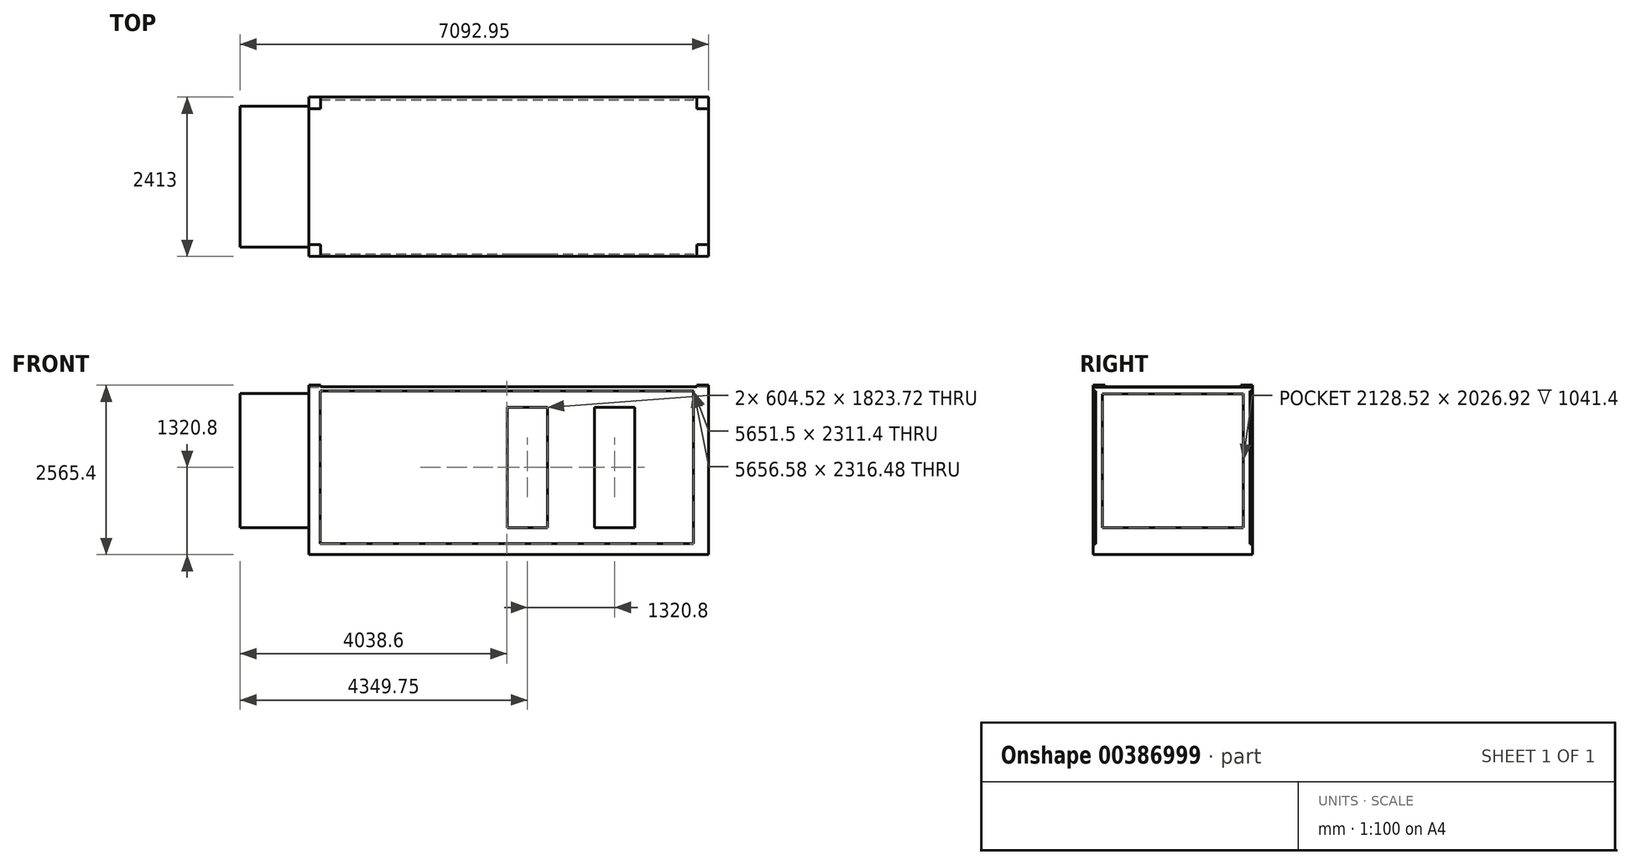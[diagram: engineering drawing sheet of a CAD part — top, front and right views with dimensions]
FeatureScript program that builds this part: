
annotation { "Feature Type Name" : "Feature", "Feature Type Description" : "" }
export const myFeature = defineFeature(function(context is Context, id is Id, definition is map)
    precondition{}
    {
        {
            var Q0;
            Q0=qCreatedBy(makeId("Front.planeOp"),FACE);
            var sketch = newSketch(context, id + "F0", { "sketchPlane" : qUnion([Q0])});
            skLineSegment(sketch, "E0.bottom", {"start": v(0, 0) * mm, "end": v(5651.5, 0) * mm, "construction": true});
            skLineSegment(sketch, "E0.top", {"start": v(0, 2311.4) * mm, "end": v(5651.5, 2311.4) * mm, "construction": true});
            skLineSegment(sketch, "E0.left", {"start": v(0, 0) * mm, "end": v(0, 2311.4) * mm, "construction": true});
            skLineSegment(sketch, "E0.right", {"start": v(5651.5, 0) * mm, "end": v(5651.5, 2311.4) * mm, "construction": true});
            skLineSegment(sketch, "E1.bottom", {"start": v(-171.45, -165.1) * mm, "end": v(5880.1, -165.1) * mm});
            skLineSegment(sketch, "E1.top", {"start": v(-171.45, 2374.9) * mm, "end": v(5880.1, 2374.9) * mm});
            skLineSegment(sketch, "E1.left", {"start": v(-171.45, -165.1) * mm, "end": v(-171.45, 2374.9) * mm});
            skLineSegment(sketch, "E1.right", {"start": v(5880.1, -165.1) * mm, "end": v(5880.1, 2374.9) * mm});
            skSolve(sketch);
        }
        {
            var Q0;
            Q0=makeQuery(id+"F0.imprint","IMPRINT",FACE,{"disambiguationData":[TD([[makeQuery(id+"F0.imprint","IMPRINT",EDGE,{"derivedFrom":sQuery(id+"F0.wireOp",EDGE,"E0.bottom")}),-1.0]])]});
            var Q1;
            Q1=makeQuery(id+"F0.imprint","IMPRINT",FACE,{"disambiguationData":[TD([[makeQuery(id+"F0.imprint","IMPRINT",EDGE,{"derivedFrom":sQuery(id+"F0.wireOp",EDGE,"E1.bottom")}),1.0]])]});
            extrude(context, id + "F1", {"entities" : qUnion([Q0, Q1]), "depth" : 2413 * mm});
        }
        {
            var Q0;
            Q0=makeQuery(id+"F1.opExtrude","CAP_FACE",FACE,{"disambiguationData":[OSD([sQuery(id+"F0.wireOp",EDGE,"E1.bottom"),sQuery(id+"F0.wireOp",EDGE,"E1.top"),sQuery(id+"F0.wireOp",EDGE,"E1.left"),sQuery(id+"F0.wireOp",EDGE,"E1.right")])],"isStart":false});
            var sketch = newSketch(context, id + "F2", { "sketchPlane" : qUnion([Q0])});
            skLineSegment(sketch, "E2.0", {"start": v(0, 2311.4) * mm, "end": v(5651.5, 2311.4) * mm});
            skLineSegment(sketch, "E3.0", {"start": v(0, 0) * mm, "end": v(5651.5, 0) * mm});
            skLineSegment(sketch, "E4.0", {"start": v(5651.5, 0) * mm, "end": v(5651.5, 2311.4) * mm});
            skLineSegment(sketch, "E5.0", {"start": v(0, 0) * mm, "end": v(0, 2311.4) * mm});
            skSolve(sketch);
        }
        {
            var Q0;
            Q0=qSketchRegion(id+"F2",true);
            extrude(context, id + "F3", {"entities" : qUnion([Q0]), "operationType" : NewBodyOperationType.REMOVE, "oppositeDirection" : true, "depth" : 38.1 * mm});
        }
        {
            var Q0;
            Q0=makeQuery(id+"F0.imprint","IMPRINT",FACE,{"disambiguationData":[TD([[makeQuery(id+"F0.imprint","IMPRINT",EDGE,{"derivedFrom":sQuery(id+"F0.wireOp",EDGE,"E1.bottom")}),1.0]])]});
            var sketch = newSketch(context, id + "F4", { "sketchPlane" : qUnion([Q0])});
            skLineSegment(sketch, "E6.0", {"start": v(0, 2311.4) * mm, "end": v(5651.5, 2311.4) * mm});
            skLineSegment(sketch, "E7.0", {"start": v(5651.5, 0) * mm, "end": v(5651.5, 2311.4) * mm});
            skLineSegment(sketch, "E8.0", {"start": v(0, 0) * mm, "end": v(5651.5, 0) * mm});
            skLineSegment(sketch, "E9.0", {"start": v(0, 0) * mm, "end": v(0, 2311.4) * mm});
            skSolve(sketch);
        }
        {
            var Q0;
            Q0=qSketchRegion(id+"F4",true);
            extrude(context, id + "F5", {"entities" : qUnion([Q0]), "operationType" : NewBodyOperationType.REMOVE, "depth" : 38.1 * mm});
        }
        {
            var Q0;
            Q0=makeQuery(id+"F3.boolean.opBoolean","COPY",FACE,{"derivedFrom":makeQuery(id+"F3.opExtrude","CAP_FACE",FACE,{"disambiguationData":[OSD([sQuery(id+"F2.wireOp",EDGE,"E2.0"),sQuery(id+"F2.wireOp",EDGE,"E3.0"),sQuery(id+"F2.wireOp",EDGE,"E4.0"),sQuery(id+"F2.wireOp",EDGE,"E5.0")])],"isStart":false})});
            var sketch = newSketch(context, id + "F6", { "sketchPlane" : qUnion([Q0])});
            skLineSegment(sketch, "E10.bottom", {"start": v(2832.1, 2070.1) * mm, "end": v(3441.7, 2070.1) * mm});
            skLineSegment(sketch, "E10.top", {"start": v(2832.1, 241.3) * mm, "end": v(3441.7, 241.3) * mm});
            skLineSegment(sketch, "E10.left", {"start": v(2832.1, 2070.1) * mm, "end": v(2832.1, 241.3) * mm});
            skLineSegment(sketch, "E10.right", {"start": v(3441.7, 2070.1) * mm, "end": v(3441.7, 241.3) * mm});
            skLineSegment(sketch, "E11.bottom", {"start": v(4152.9, 2070.1) * mm, "end": v(4762.5, 2070.1) * mm});
            skLineSegment(sketch, "E11.top", {"start": v(4152.9, 241.3) * mm, "end": v(4762.5, 241.3) * mm});
            skLineSegment(sketch, "E11.left", {"start": v(4152.9, 2070.1) * mm, "end": v(4152.9, 241.3) * mm});
            skLineSegment(sketch, "E11.right", {"start": v(4762.5, 2070.1) * mm, "end": v(4762.5, 241.3) * mm});
            skLineSegment(sketch, "E12", {"start": v(3267.34, 2311.4) * mm, "end": v(3267.34, 2070.1) * mm, "construction": true});
            skLineSegment(sketch, "E13", {"start": v(4451.93, 241.3) * mm, "end": v(4451.93, 0) * mm, "construction": true});
            skLineSegment(sketch, "E14", {"start": v(2825.75, 2311.4) * mm, "end": v(2825.75, 0) * mm, "construction": true});
            skSolve(sketch);
        }
        {
            var Q0;
            Q0=qSketchRegion(id+"F6",true);
            extrude(context, id + "F7", {"entities" : qUnion([Q0]), "operationType" : NewBodyOperationType.ADD, "depth" : 25.4 * mm});
        }
        {
            var Q0;
            Q0=makeQuery(id+"F1.opExtrude","SWEPT_FACE",FACE,{"disambiguationData":[OSD([sQuery(id+"F0.wireOp",EDGE,"E1.left")])]});
            var sketch = newSketch(context, id + "F8", { "sketchPlane" : qUnion([Q0])});
            skLineSegment(sketch, "E15.bottom", {"start": v(139.7, 2273.3) * mm, "end": v(2273.3, 2273.3) * mm});
            skLineSegment(sketch, "E15.top", {"start": v(139.7, 241.3) * mm, "end": v(2273.3, 241.3) * mm});
            skLineSegment(sketch, "E15.left", {"start": v(139.7, 2273.3) * mm, "end": v(139.7, 241.3) * mm});
            skLineSegment(sketch, "E15.right", {"start": v(2273.3, 2273.3) * mm, "end": v(2273.3, 241.3) * mm});
            skSolve(sketch);
        }
        {
            var Q0;
            Q0=qSketchRegion(id+"F8",true);
            extrude(context, id + "F9", {"entities" : qUnion([Q0]), "operationType" : NewBodyOperationType.ADD, "depth" : 1041.4 * mm});
        }
        {
            var Q0;
            Q0=makeQuery(id+"F1.opExtrude","SWEPT_FACE",FACE,{"disambiguationData":[OSD([sQuery(id+"F0.wireOp",EDGE,"E1.top")])]});
            var sketch = newSketch(context, id + "F10", { "sketchPlane" : qUnion([Q0])});
            skLineSegment(sketch, "E16.bottom", {"start": v(-171.45, -2413) * mm, "end": v(6.35, -2413) * mm});
            skLineSegment(sketch, "E16.top", {"start": v(-171.45, -2235.2) * mm, "end": v(6.35, -2235.2) * mm});
            skLineSegment(sketch, "E16.left", {"start": v(-171.45, -2413) * mm, "end": v(-171.45, -2235.2) * mm});
            skLineSegment(sketch, "E16.right", {"start": v(6.35, -2413) * mm, "end": v(6.35, -2235.2) * mm});
            skLineSegment(sketch, "E17.bottom", {"start": v(-171.45, 0) * mm, "end": v(6.35, 0) * mm});
            skLineSegment(sketch, "E17.top", {"start": v(-171.45, -177.8) * mm, "end": v(6.35, -177.8) * mm});
            skLineSegment(sketch, "E17.left", {"start": v(-171.45, 0) * mm, "end": v(-171.45, -177.8) * mm});
            skLineSegment(sketch, "E17.right", {"start": v(6.35, 0) * mm, "end": v(6.35, -177.8) * mm});
            skLineSegment(sketch, "E18.bottom", {"start": v(5880.1, 0) * mm, "end": v(5702.3, 0) * mm});
            skLineSegment(sketch, "E18.top", {"start": v(5880.1, -177.8) * mm, "end": v(5702.3, -177.8) * mm});
            skLineSegment(sketch, "E18.left", {"start": v(5880.1, 0) * mm, "end": v(5880.1, -177.8) * mm});
            skLineSegment(sketch, "E18.right", {"start": v(5702.3, 0) * mm, "end": v(5702.3, -177.8) * mm});
            skLineSegment(sketch, "E19.bottom", {"start": v(5880.1, -2413) * mm, "end": v(5702.3, -2413) * mm});
            skLineSegment(sketch, "E19.top", {"start": v(5880.1, -2235.2) * mm, "end": v(5702.3, -2235.2) * mm});
            skLineSegment(sketch, "E19.left", {"start": v(5880.1, -2413) * mm, "end": v(5880.1, -2235.2) * mm});
            skLineSegment(sketch, "E19.right", {"start": v(5702.3, -2413) * mm, "end": v(5702.3, -2235.2) * mm});
            skSolve(sketch);
        }
        {
            var Q0;
            Q0=qSketchRegion(id+"F10",true);
            extrude(context, id + "F11", {"entities" : qUnion([Q0]), "operationType" : NewBodyOperationType.ADD, "depth" : 25.4 * mm});
        }
        {
            var Q0;
            Q0=makeQuery(id+"F11.boolean.opBoolean","MERGE",FACE,{"derivedFrom":[makeQuery(id+"F1.opExtrude","CAP_FACE",FACE,{"disambiguationData":[OSD([sQuery(id+"F0.wireOp",EDGE,"E1.bottom"),sQuery(id+"F0.wireOp",EDGE,"E1.top"),sQuery(id+"F0.wireOp",EDGE,"E1.left"),sQuery(id+"F0.wireOp",EDGE,"E1.right")])],"isStart":false}),makeQuery(id+"F11.opExtrude","SWEPT_FACE",FACE,{"disambiguationData":[OSD([sQuery(id+"F10.wireOp",EDGE,"E16.bottom")])]}),makeQuery(id+"F11.opExtrude","SWEPT_FACE",FACE,{"disambiguationData":[OSD([sQuery(id+"F10.wireOp",EDGE,"E19.bottom")])]})]});
            var sketch = newSketch(context, id + "F12", { "sketchPlane" : qUnion([Q0])});
            skLineSegment(sketch, "E20", {"start": v(5880.1, -12.7) * mm, "end": v(7404.1, -165.1) * mm});
            skLineSegment(sketch, "E21", {"start": v(7404.1, -165.1) * mm, "end": v(7404.1, -114.05) * mm});
            skLineSegment(sketch, "E22", {"start": v(7404.1, -114.05) * mm, "end": v(5880.1, 38.35) * mm});
            skLineSegment(sketch, "E23", {"start": v(5880.1, 38.35) * mm, "end": v(5880.1, -12.7) * mm});
            skSolve(sketch);
        }
        {
            var Q0;
            {var subQ0=sQuery(id+"F10.wireOp",EDGE,"E19.left");var subQ5=sQuery(id+"F0.wireOp",EDGE,"E1.right");var subQ7=sQuery(id+"F0.wireOp",EDGE,"E1.top");var subQ9=sQuery(id+"F10.wireOp",EDGE,"E18.left");Q0=makeQuery(id+"FrM0suulV1ynvPr_1.boolean.opBoolean","SPLIT",FACE,{"disambiguationData":[TD([makeQuery(id+"F1.opExtrude","SWEPT_FACE",FACE,{"disambiguationData":[OSD([subQ7])]})])],"derivedFrom":makeQuery(id+"F11.boolean.opBoolean","MERGE",FACE,{"derivedFrom":[makeQuery(id+"F1.opExtrude","SWEPT_FACE",FACE,{"disambiguationData":[OSD([subQ5])]}),makeQuery(id+"F11.opExtrude","SWEPT_FACE",FACE,{"disambiguationData":[OSD([subQ9])]}),makeQuery(id+"F11.opExtrude","SWEPT_FACE",FACE,{"disambiguationData":[OSD([subQ0])]})]})});}
            shell(context, id + "F13", {"entities" : qUnion([Q0]), "thickness" : 2.54 * mm});
        }
        {
            var Q0;
            Q0=makeQuery(id+"F7.opExtrude","CAP_FACE",FACE,{"disambiguationData":[OSD([sQuery(id+"F6.wireOp",EDGE,"E10.bottom"),sQuery(id+"F6.wireOp",EDGE,"E10.top"),sQuery(id+"F6.wireOp",EDGE,"E10.left"),sQuery(id+"F6.wireOp",EDGE,"E10.right")])],"isStart":false});
            extrude(context, id + "F14", {"entities" : qUnion([Q0]), "operationType" : NewBodyOperationType.REMOVE, "oppositeDirection" : true, "depth" : 25.4 * mm});
        }
        {
            var Q0;
            Q0=makeQuery(id+"F7.opExtrude","CAP_FACE",FACE,{"disambiguationData":[OSD([sQuery(id+"F6.wireOp",EDGE,"E11.bottom"),sQuery(id+"F6.wireOp",EDGE,"E11.top"),sQuery(id+"F6.wireOp",EDGE,"E11.left"),sQuery(id+"F6.wireOp",EDGE,"E11.right")])],"isStart":false});
            extrude(context, id + "F15", {"entities" : qUnion([Q0]), "operationType" : NewBodyOperationType.REMOVE, "oppositeDirection" : true, "depth" : 25.4 * mm});
        }
    });
